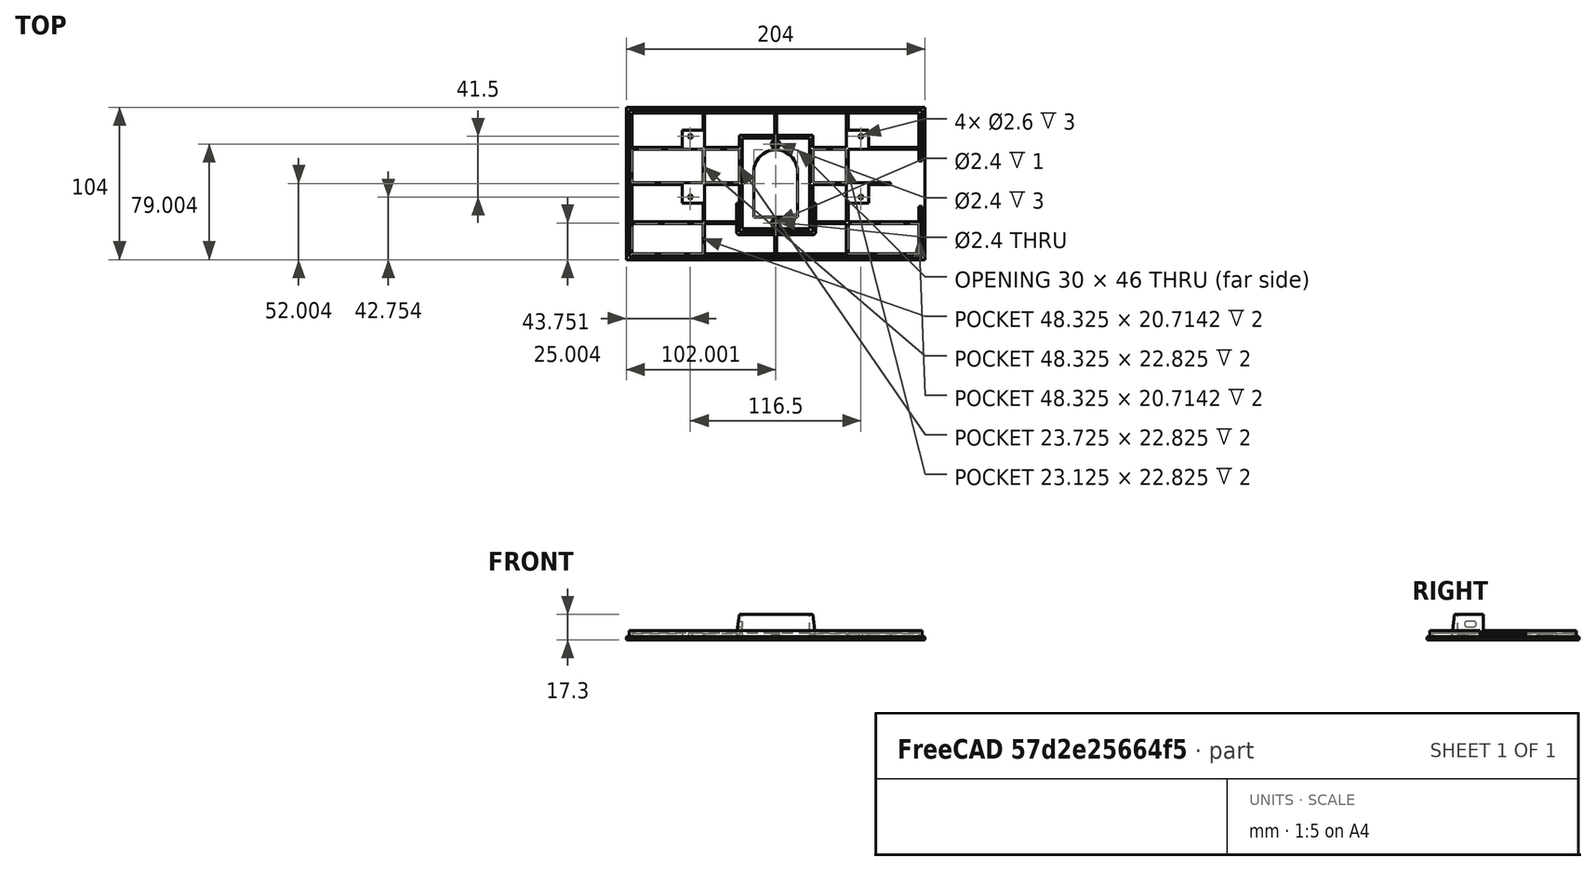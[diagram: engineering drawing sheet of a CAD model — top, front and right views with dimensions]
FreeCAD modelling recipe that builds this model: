
FCSTD DOCUMENT  (FreeCAD 0.18.3R)
Label: lamp.base.top.230V.flat.shortside
License: All rights reserved
LicenseURL: http://en.wikipedia.org/wiki/All_rights_reserved
objects: Part::Extrusion×29, Part::Part2DObjectPython×22, Part::MultiFuse×11, Part::Cut×11, Part::Feature×9, Part::Cone×1
note: 83 computed .brp shape members not serialized (recipe doc carries the construction recipe); baked Part::Feature solids carry a one-line shape summary decoded from their .brp

FEATURE [Part::Part2DObjectPython] Circle  # Draft 2D object (typed FeaturePython)
  FirstAngle = 0
  LastAngle = 0
  MakeFace = true
  Placement = pos=(-178.299,-608.196,8.99975) rot=(1,0,0;3.14159rad)
  Radius = 1.3
FEATURE [Part::Part2DObjectPython] Circle001  # Draft 2D object (typed FeaturePython)
  FirstAngle = 0
  LastAngle = 0
  MakeFace = true
  Placement = pos=(-178.299,-649.696,8.99975) rot=(1,0,0;3.14159rad)
  Radius = 1.3
FEATURE [Part::Part2DObjectPython] Circle002  # Draft 2D object (typed FeaturePython)
  FirstAngle = 0
  LastAngle = 0
  MakeFace = true
  Placement = pos=(-61.7989,-608.196,8.99975) rot=(1,0,0;3.14159rad)
  Radius = 1.3
FEATURE [Part::Part2DObjectPython] Circle003  # Draft 2D object (typed FeaturePython)
  FirstAngle = 0
  LastAngle = 0
  MakeFace = true
  Placement = pos=(-61.7989,-649.696,8.99975) rot=(1,0,0;3.14159rad)
  Radius = 1.3
FEATURE [Part::Extrusion] Extrude
  Base = -> Circle002
  Dir = (0,2e-15,-1)
  DirMode = 2
  FaceMakerClass = Part::FaceMakerBullseye
  LengthFwd = -4
  LengthRev = 0
  Placement = pos=(0,0,-1) rot=(0,0,1;0rad)
  Solid = false
  Symmetric = false
FEATURE [Part::Extrusion] Extrude001
  Base = -> Circle003
  Dir = (0,2e-15,-1)
  DirMode = 2
  FaceMakerClass = Part::FaceMakerBullseye
  LengthFwd = -4
  LengthRev = 0
  Placement = pos=(0,0,-1) rot=(0,0,1;0rad)
  Solid = false
  Symmetric = false
FEATURE [Part::Extrusion] Extrude002
  Base = -> Circle
  Dir = (0,2e-15,-1)
  DirMode = 2
  FaceMakerClass = Part::FaceMakerBullseye
  LengthFwd = -4
  LengthRev = 0
  Placement = pos=(0,0,-1) rot=(0,0,1;0rad)
  Solid = false
  Symmetric = false
FEATURE [Part::Extrusion] Extrude003
  Base = -> Circle001
  Dir = (0,2e-15,-1)
  DirMode = 2
  FaceMakerClass = Part::FaceMakerBullseye
  LengthFwd = -4
  LengthRev = 0
  Placement = pos=(0,0,-1) rot=(0,0,1;0rad)
  Solid = false
  Symmetric = false
FEATURE [Part::Part2DObjectPython] Rectangle002  # Draft 2D object (typed FeaturePython)
  ChamferSize = 0
  Columns = 1
  FilletRadius = 0
  Height = 15
  Length = 50
  MakeFace = true
  Placement = pos=(-144.749,-673.446,9) rot=(1,0,0;1.5708rad)
  Rows = 1
FEATURE [Part::Extrusion] Extrusion001
  Base = -> Rectangle002
  Dir = (5e-16,2,-4e-16)
  DirMode = 0
  FaceMakerClass = Part::FaceMakerBullseye
  LengthFwd = 0
  LengthRev = 0
  Solid = true
  Symmetric = false
FEATURE [Part::Feature] Fusion076001  label="Fusion091"
  Placement = pos=(-6.79071,-148.437,16) rot=(0,0,1;0rad)
  shape: bbox 204 x 104 x 6 mm, 190 faces, 2 solids (baked)
FEATURE [Part::Part2DObjectPython] Circle004  # Draft 2D object (typed FeaturePython)
  FirstAngle = 0
  LastAngle = 0
  MakeFace = true
  Placement = pos=(-144.749,-658.571,17.5) rot=(0.57735,-0.57735,-0.57735;2.0944rad)
  Radius = 2
FEATURE [Part::Part2DObjectPython] Circle005  # Draft 2D object (typed FeaturePython)
  FirstAngle = 0
  LastAngle = 0
  MakeFace = true
  Placement = pos=(-144.749,-662.571,17.5) rot=(0.57735,-0.57735,-0.57735;2.0944rad)
  Radius = 2
FEATURE [Part::Part2DObjectPython] Rectangle007  # Draft 2D object (typed FeaturePython)
  ChamferSize = 0
  Columns = 1
  FilletRadius = 0
  Height = 4
  Length = 4
  MakeFace = true
  Placement = pos=(-144.749,-658.571,15.5) rot=(0.57735,-0.57735,-0.57735;2.0944rad)
  Rows = 1
FEATURE [Part::Extrusion] Extrude005
  Base = -> Circle004
  Dir = (-1,0,0)
  DirMode = 2
  FaceMakerClass = Part::FaceMakerBullseye
  LengthFwd = -10
  LengthRev = 0
  Solid = false
  Symmetric = false
FEATURE [Part::Extrusion] Extrude006
  Base = -> Circle005
  Dir = (-1,0,0)
  DirMode = 2
  FaceMakerClass = Part::FaceMakerBullseye
  LengthFwd = -10
  LengthRev = 0
  Solid = false
  Symmetric = false
FEATURE [Part::Extrusion] Extrude007
  Base = -> Rectangle007
  Dir = (-1,0,0)
  DirMode = 2
  FaceMakerClass = Part::FaceMakerBullseye
  LengthFwd = -10
  LengthRev = 0
  Solid = false
  Symmetric = false
FEATURE [Part::MultiFuse] Fusion
  Placement = pos=(0,-2.125,-4e-15) rot=(0,0,1;0rad)
  Shapes = -> [Extrude005,Extrude007,Extrude006]
FEATURE [Part::Part2DObjectPython] Rectangle008  # Draft 2D object (typed FeaturePython)
  ChamferSize = 0
  Columns = 1
  FilletRadius = 0
  Height = 17.5
  Length = 2
  MakeFace = true
  Placement = pos=(-96.7489,-671.446,11) rot=(0,0,1;0rad)
  Rows = 1
  Support = -> [Fusion076001]
FEATURE [Part::Extrusion] Extrusion002
  Base = -> Rectangle008
  Dir = (-1.15e-14,1.4e-15,13)
  DirMode = 0
  FaceMakerClass = Part::FaceMakerBullseye
  LengthFwd = 0
  LengthRev = 0
  Solid = true
  Symmetric = false
FEATURE [Part::Part2DObjectPython] Rectangle009  # Draft 2D object (typed FeaturePython)
  ChamferSize = 0
  Columns = 1
  FilletRadius = 0
  Height = 17.5
  Length = 2
  MakeFace = true
  Placement = pos=(-144.749,-671.446,11) rot=(0,0,1;0rad)
  Rows = 1
FEATURE [Part::Extrusion] Extrusion003
  Base = -> Rectangle009
  Dir = (-1.15e-14,1.4e-15,13)
  DirMode = 0
  FaceMakerClass = Part::FaceMakerBullseye
  LengthFwd = 0
  LengthRev = 0
  Solid = true
  Symmetric = false
FEATURE [Part::Cut] Cut
  Base = -> Extrusion003
  Tool = -> Fusion
FEATURE [Part::MultiFuse] Fusion076002
  Shapes = -> [Cut,Extrusion001,Extrusion002]
FEATURE [Part::Part2DObjectPython] Rectangle011  # Draft 2D object (typed FeaturePython)
  ChamferSize = 0
  Columns = 1
  FilletRadius = 0
  Height = 31
  Length = 2
  MakeFace = true
  Placement = pos=(-21.9989,-655.946,13) rot=(0,0,1;0rad)
  Rows = 1
  Support = -> [Fusion076001]
FEATURE [Part::Extrusion] Extrude009
  Base = -> Rectangle011
  Dir = (-9e-16,1e-16,1)
  DirMode = 2
  FaceMakerClass = Part::FaceMakerBullseye
  LengthFwd = -4
  LengthRev = 0
  Solid = false
  Symmetric = false
FEATURE [Part::Cut] Cut001
  Base = -> Fusion076001
  Tool = -> Extrude009
FEATURE [Part::Part2DObjectPython] Rectangle012  # Draft 2D object (typed FeaturePython)
  ChamferSize = 0
  Columns = 1
  FilletRadius = 0
  Height = 2
  Length = 19.5
  MakeFace = true
  Placement = pos=(-41.4989,-641.046,9) rot=(1,0,0;1.5708rad)
  Rows = 1
  Support = -> [Cut001]
FEATURE [Part::Extrusion] Extrusion004
  Base = -> Rectangle012
  Dir = (1e-16,1.2,-3e-16)
  DirMode = 0
  FaceMakerClass = Part::FaceMakerBullseye
  LengthFwd = 0
  LengthRev = 0
  Solid = true
  Symmetric = false
FEATURE [Part::Cut] Cut002
  Base = -> Cut001
  Tool = -> Extrusion004
FEATURE [Part::Part2DObjectPython] Rectangle013  # Draft 2D object (typed FeaturePython)
  ChamferSize = 0
  Columns = 1
  FilletRadius = 0
  Height = 12.9
  Length = 14.025
  MakeFace = true
  Placement = pos=(-70.4239,-653.946,11) rot=(0,0,1;0rad)
  Rows = 1
FEATURE [Part::Extrusion] Extrusion005
  Base = -> Rectangle013
  Dir = (0,0,-2.00025)
  DirMode = 0
  FaceMakerClass = Part::FaceMakerBullseye
  LengthFwd = 0
  LengthRev = 0
  Solid = true
  Symmetric = false
FEATURE [Part::Part2DObjectPython] Rectangle014  # Draft 2D object (typed FeaturePython)
  ChamferSize = 0
  Columns = 1
  FilletRadius = 0
  Height = 11.875
  Length = 14.025
  MakeFace = true
  Placement = pos=(-70.4239,-615.821,11) rot=(0,0,1;0rad)
  Rows = 1
FEATURE [Part::Extrusion] Extrusion006
  Base = -> Rectangle014
  Dir = (0,0,-2.00025)
  DirMode = 0
  FaceMakerClass = Part::FaceMakerBullseye
  LengthFwd = 0
  LengthRev = 0
  Solid = true
  Symmetric = false
FEATURE [Part::Part2DObjectPython] Rectangle015  # Draft 2D object (typed FeaturePython)
  ChamferSize = 0
  Columns = 1
  FilletRadius = 0
  Height = 11.875
  Length = 14.025
  MakeFace = true
  Placement = pos=(-183.699,-615.821,11) rot=(0,0,1;0rad)
  Rows = 1
FEATURE [Part::Extrusion] Extrusion007
  Base = -> Rectangle015
  Dir = (0,0,-2.00025)
  DirMode = 0
  FaceMakerClass = Part::FaceMakerBullseye
  LengthFwd = 0
  LengthRev = 0
  Solid = true
  Symmetric = false
FEATURE [Part::Part2DObjectPython] Rectangle016  # Draft 2D object (typed FeaturePython)
  ChamferSize = 0
  Columns = 1
  FilletRadius = 0
  Height = 12.9
  Length = 14.025
  MakeFace = true
  Placement = pos=(-183.699,-653.946,11) rot=(0,0,1;0rad)
  Rows = 1
FEATURE [Part::Extrusion] Extrusion008
  Base = -> Rectangle016
  Dir = (0,0,-2.00025)
  DirMode = 0
  FaceMakerClass = Part::FaceMakerBullseye
  LengthFwd = 0
  LengthRev = 0
  Solid = true
  Symmetric = false
FEATURE [Part::MultiFuse] Fusion076003
  Shapes = -> [Extrusion007,Extrusion008,Extrusion005,Extrusion006]
FEATURE [Part::MultiFuse] Fusion076004
  Shapes = -> [Fusion076003,Cut002]
FEATURE [Part::Cut] Cut003
  Base = -> Fusion076004
  Tool = -> Extrude002
FEATURE [Part::Cut] Cut004
  Base = -> Cut003
  Tool = -> Extrude003
FEATURE [Part::Cut] Cut005
  Base = -> Cut004
  Tool = -> Extrude001
FEATURE [Part::Cut] Cut006
  Base = -> Cut005
  Tool = -> Extrude
FEATURE [Part::Part2DObjectPython] Wire001  # Draft 2D object (typed FeaturePython)
  ChamferSize = 0
  Closed = true
  End = (-144.749,-673.446,9)
  FilletRadius = 0
  Length = 32.1327
  MakeFace = true
  Placement = pos=(-146.749,-673.446,9) rot=(0,0,1;0rad)
  Points = (3) [(0,0,0),(2,0,15),(2,0,0)]
  Start = (-146.749,-673.446,9)
  Subdivisions = 0
FEATURE [Part::Extrusion] Extrusion009
  Base = -> Wire001
  Dir = (-6e-16,19.5,0)
  DirMode = 0
  FaceMakerClass = Part::FaceMakerBullseye
  LengthFwd = 0
  LengthRev = 0
  Solid = true
  Symmetric = false
FEATURE [Part::Part2DObjectPython] Wire002  # Draft 2D object (typed FeaturePython)
  ChamferSize = 0
  Closed = true
  End = (-94.7489,-673.446,9)
  FilletRadius = 0
  Length = 32.1327
  MakeFace = true
  Placement = pos=(-94.7489,-673.446,24) rot=(0,0,1;0rad)
  Points = (3) [(0,0,0),(2,0,-15),(0,0,-15)]
  Start = (-94.7489,-673.446,24)
  Subdivisions = 0
FEATURE [Part::Extrusion] Extrusion010
  Base = -> Wire002
  Dir = (-6e-16,19.5,0)
  DirMode = 0
  FaceMakerClass = Part::FaceMakerBullseye
  LengthFwd = 0
  LengthRev = 0
  Solid = true
  Symmetric = false
FEATURE [Part::Part2DObjectPython] Wire003  # Draft 2D object (typed FeaturePython)
  ChamferSize = 0
  Closed = true
  End = (-94.7489,-675.446,9)
  FilletRadius = 0
  Length = 32.1327
  MakeFace = true
  Placement = pos=(-94.7489,-673.446,24) rot=(0,0,1;0rad)
  Points = (3) [(0,0,0),(0,0,-15),(0,-2,-15)]
  Start = (-94.7489,-673.446,24)
  Subdivisions = 0
FEATURE [Part::Extrusion] Extrusion011
  Base = -> Wire003
  Dir = (-50,-1.5e-15,0)
  DirMode = 0
  FaceMakerClass = Part::FaceMakerBullseye
  LengthFwd = 0
  LengthRev = 0
  Solid = true
  Symmetric = false
FEATURE [Part::Cone] Cone
  Angle = 360
  AttacherType = Attacher::AttachEngine3D
  Height = 15
  Placement = pos=(-94.7489,-673.446,9) rot=(0,0,1;0rad)
  Radius1 = 2
  Radius2 = 0
FEATURE [Part::Feature] Cone001
  Placement = pos=(-144.749,-673.446,9) rot=(0,0,1;0rad)
  shape: bbox 4 x 4 x 15 mm, 2 faces (baked)
FEATURE [Part::MultiFuse] Fusion076005
  Shapes = -> [Extrusion009,Cone001,Extrusion011,Cone,Extrusion010]
FEATURE [Part::MultiFuse] Fusion076006
  Shapes = -> [Fusion076005,Fusion076002]
FEATURE [Part::MultiFuse] Fusion076007
  Shapes = -> [Cut006,Fusion076006]
FEATURE [Part::Part2DObjectPython] Rectangle017  # Draft 2D object (typed FeaturePython)
  ChamferSize = 0
  Columns = 1
  FilletRadius = 0
  Height = 4
  Length = 4
  MakeFace = true
  Placement = pos=(-142.749,-664.696,15.5) rot=(0.57735,0.57735,0.57735;2.0944rad)
  Rows = 1
  Support = -> [Fusion076007]
FEATURE [Part::Part2DObjectPython] Circle006  # Draft 2D object (typed FeaturePython)
  FirstAngle = 0
  LastAngle = 0
  MakeFace = true
  Placement = pos=(-142.749,-660.696,17.5) rot=(0.57735,0.57735,0.57735;2.0944rad)
  Radius = 2
FEATURE [Part::Part2DObjectPython] Circle007  # Draft 2D object (typed FeaturePython)
  FirstAngle = 0
  LastAngle = 0
  MakeFace = true
  Placement = pos=(-142.749,-664.696,17.5) rot=(0.57735,0.57735,0.57735;2.0944rad)
  Radius = 2
FEATURE [Part::Extrusion] Extrude010
  Base = -> Rectangle017
  Dir = (1,0,0)
  DirMode = 2
  FaceMakerClass = Part::FaceMakerBullseye
  LengthFwd = -10
  LengthRev = 0
  Solid = false
  Symmetric = false
FEATURE [Part::Extrusion] Extrude011
  Base = -> Circle006
  Dir = (1,0,0)
  DirMode = 2
  FaceMakerClass = Part::FaceMakerBullseye
  LengthFwd = -10
  LengthRev = 0
  Solid = false
  Symmetric = false
FEATURE [Part::Extrusion] Extrude012
  Base = -> Circle007
  Dir = (1,0,0)
  DirMode = 2
  FaceMakerClass = Part::FaceMakerBullseye
  LengthFwd = -10
  LengthRev = 0
  Solid = false
  Symmetric = false
FEATURE [Part::MultiFuse] Fusion076008
  Shapes = -> [Extrude012,Extrude011,Extrude010]
FEATURE [Part::Cut] Cut007
  Base = -> Fusion076007
  Tool = -> Fusion076008
FEATURE [Part::Feature] Face
  Placement = pos=(-6.79071,-148.437,16) rot=(0,0,1;0rad)
  shape: bbox 204 x 104 x 3e-07 mm, 1 faces, 0 solids (baked)
FEATURE [Part::Extrusion] Extrusion012
  Base = -> Face
  Dir = (0,0,-0.3)
  DirMode = 0
  FaceMakerClass = Part::FaceMakerBullseye
  LengthFwd = 0
  LengthRev = 0
  Solid = true
  Symmetric = false
FEATURE [Part::MultiFuse] Fusion076009
  Shapes = -> [Extrusion012,Cut007]
FEATURE [Part::Feature] Face001
  Placement = pos=(-6.79071,-148.437,16) rot=(0,0,1;0rad)
  shape: bbox 2e-07 x 100.1 x 4 mm, 1 faces, 0 solids (baked)
FEATURE [Part::Extrusion] Extrusion013
  Base = -> Face001
  Dir = (0.1,0,0)
  DirMode = 0
  FaceMakerClass = Part::FaceMakerBullseye
  LengthFwd = 0
  LengthRev = 0
  Solid = true
  Symmetric = false
FEATURE [Part::Feature] Face003
  Placement = pos=(-6.79071,-148.437,16) rot=(0,0,1;0rad)
  shape: bbox 3e-07 x 96.1 x 4 mm, 1 faces, 0 solids (baked)
FEATURE [Part::Extrusion] Extrusion014
  Base = -> Face003
  Dir = (0.1,0,0)
  DirMode = 0
  FaceMakerClass = Part::FaceMakerBullseye
  LengthFwd = 0
  LengthRev = 0
  Solid = true
  Symmetric = false
FEATURE [Part::Feature] Face004
  shape: bbox 3e-07 x 32.55 x 4 mm, 1 faces, 0 solids (baked)
FEATURE [Part::Extrusion] Extrusion015
  Base = -> Face004
  Dir = (-0.1,0,0)
  DirMode = 0
  FaceMakerClass = Part::FaceMakerBullseye
  LengthFwd = 0
  LengthRev = 0
  Solid = true
  Symmetric = false
FEATURE [Part::Feature] Face005
  shape: bbox 3e-07 x 32.55 x 4 mm, 1 faces, 0 solids (baked)
FEATURE [Part::Extrusion] Extrusion016
  Base = -> Face005
  Dir = (-0.1,0,0)
  DirMode = 0
  FaceMakerClass = Part::FaceMakerBullseye
  LengthFwd = 0
  LengthRev = 0
  Solid = true
  Symmetric = false
FEATURE [Part::Feature] Face006
  shape: bbox 2e-07 x 34.55 x 4 mm, 1 faces, 0 solids (baked)
FEATURE [Part::Extrusion] Extrusion017
  Base = -> Face006
  Dir = (-0.1,0,0)
  DirMode = 0
  FaceMakerClass = Part::FaceMakerBullseye
  LengthFwd = 0
  LengthRev = 0
  Solid = true
  Symmetric = false
FEATURE [Part::Feature] Face008
  shape: bbox 2e-07 x 34.55 x 4 mm, 1 faces, 0 solids (baked)
FEATURE [Part::Extrusion] Extrusion018
  Base = -> Face008
  Dir = (-0.1,0,0)
  DirMode = 0
  FaceMakerClass = Part::FaceMakerBullseye
  LengthFwd = 0
  LengthRev = 0
  Solid = true
  Symmetric = false
FEATURE [Part::Cut] Cut008
  Base = -> Fusion076009
  Tool = -> Extrusion018
FEATURE [Part::Cut] Cut009
  Base = -> Cut008
  Tool = -> Extrusion017
FEATURE [Part::MultiFuse] Fusion076010
  Shapes = -> [Extrusion015,Extrusion016,Cut009]
FEATURE [Part::MultiFuse] Fusion076011
  Shapes = -> [Extrusion014,Fusion076010]
FEATURE [Part::Cut] Cut010
  Base = -> Fusion076011
  Tool = -> Extrusion013
